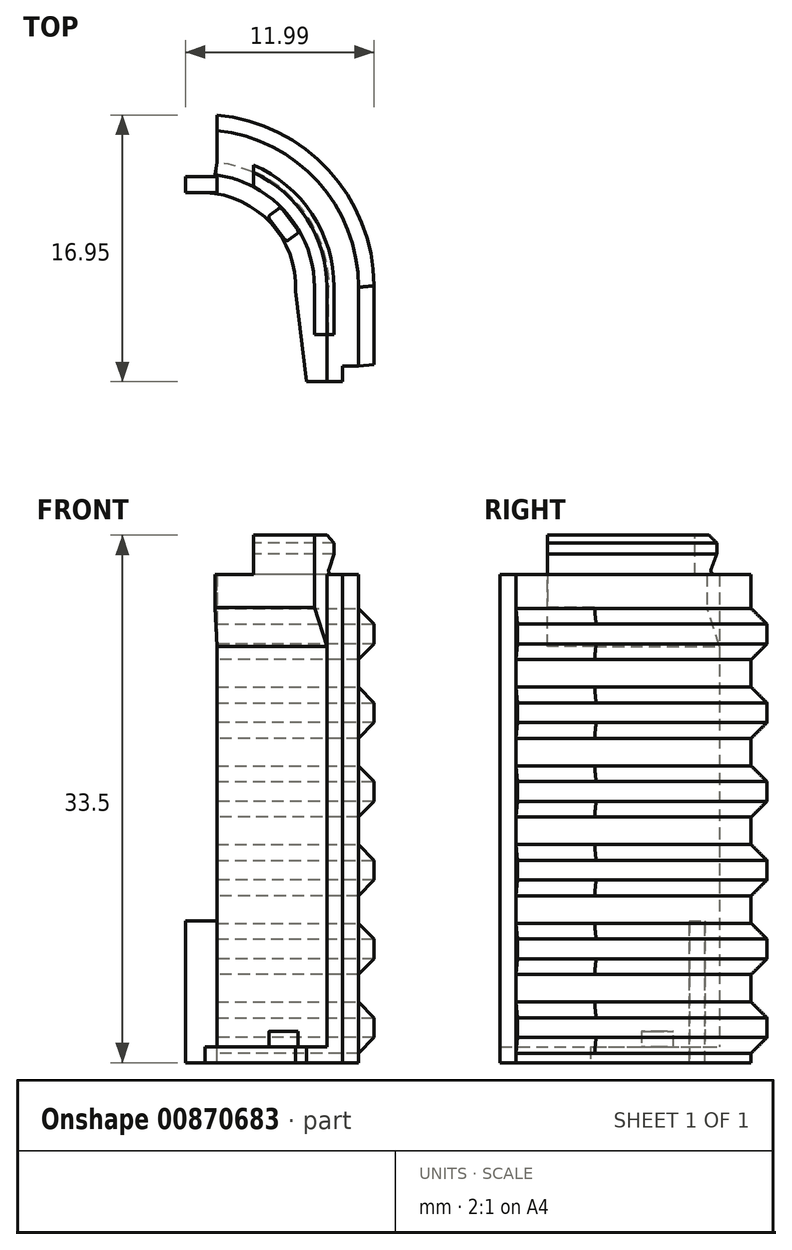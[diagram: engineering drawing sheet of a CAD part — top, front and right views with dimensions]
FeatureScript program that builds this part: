
annotation { "Feature Type Name" : "Feature", "Feature Type Description" : "" }
export const myFeature = defineFeature(function(context is Context, id is Id, definition is map)
    precondition{}
    {
        {
            var Q0;
            Q0=qCreatedBy(makeId("Top.planeOp"),FACE);
            var sketch = newSketch(context, id + "F0", { "sketchPlane" : qUnion([Q0])});
            skArc(sketch, "E0", {"start": v(10, 0) * mm, "mid": v(7.07, 7.07) * mm, "end": v(0, 10) * mm});
            skArc(sketch, "E1", {"start": v(8, 0) * mm, "mid": v(5.66, 5.66) * mm, "end": v(0, 8) * mm});
            skLineSegment(sketch, "E2", {"start": v(0, 8) * mm, "end": v(0, 10) * mm});
            skLineSegment(sketch, "E3.0", {"start": v(8, -5) * mm, "end": v(10, -5) * mm});
            skLineSegment(sketch, "E4", {"start": v(8, 0) * mm, "end": v(8, -5) * mm});
            skLineSegment(sketch, "E5", {"start": v(10, 0) * mm, "end": v(10, -5) * mm});
            skSolve(sketch);
        }
        {
            var Q0;
            Q0=makeQuery(id+"F0.imprint","IMPRINT",FACE,{"disambiguationData":[TD([[makeQuery(id+"F0.imprint","IMPRINT",EDGE,{"derivedFrom":sQuery(id+"F0.wireOp",EDGE,"E0")}),1.0]])]});
            extrude(context, id + "F1", {"entities" : qUnion([Q0]), "depth" : 31 * mm, "offsetDistance" : 25 * mm});
        }
        {
            var Q0;
            {var subQ0=sQuery(id+"F0.wireOp",EDGE,"E1");Q0=makeQuery(id+"FjqXergtBeOg1T9_1.boolean.opBoolean","MERGE",FACE,{"derivedFrom":[makeQuery(id+"F1.opExtrude","CAP_FACE",FACE,{"disambiguationData":[OSD([sQuery(id+"F0.wireOp",EDGE,"E0"),subQ0,sQuery(id+"F0.wireOp",EDGE,"E2"),sQuery(id+"F0.wireOp",EDGE,"4YHJIpGK-HOE4-qftu-6N1K-RQKpWv2yEjac")])],"isStart":false}),makeQuery(id+"FjqXergtBeOg1T9_1.opSweep","SWEPT_FACE",FACE,{"disambiguationData":[OSD([subQ0,sQuery(id+"F456tpTZeAtuVHj_1.wireOp",EDGE,"sk94qZU0-1xnX-XY7q-ALrQ-k9b9ehyhfIlW")])]})]});}
            var sketch = newSketch(context, id + "F2", { "sketchPlane" : qUnion([Q0])});
            skLineSegment(sketch, "E6.bottom", {"start": v(0, 10) * mm, "end": v(1, 10) * mm});
            skLineSegment(sketch, "E6.top", {"start": v(0, 9) * mm, "end": v(1, 9) * mm});
            skLineSegment(sketch, "E6.left", {"start": v(0, 10) * mm, "end": v(0, 9) * mm});
            skLineSegment(sketch, "E6.right", {"start": v(1, 10) * mm, "end": v(1, 9) * mm});
            skSolve(sketch);
        }
        {
            var Q0;
            {var subQ0=sQuery(id+"F2.wireOp",EDGE,"E6.top");Q0=makeQuery(id+"F2.imprint","IMPRINT",FACE,{"disambiguationData":[TD([[makeQuery(id+"F2.imprint","IMPRINT",EDGE,{"derivedFrom":subQ0}),1.0]])]});}
            extrude(context, id + "F3", {"entities" : qUnion([Q0]), "operationType" : NewBodyOperationType.REMOVE, "oppositeDirection" : true, "depth" : 33.9 * mm, "offsetDistance" : 25 * mm});
        }
        {
            var Q0;
            {var subQ0=sQuery(id+"F0.wireOp",EDGE,"E1");Q0=makeQuery(id+"FjqXergtBeOg1T9_1.boolean.opBoolean","MERGE",FACE,{"derivedFrom":[makeQuery(id+"F1.opExtrude","CAP_FACE",FACE,{"disambiguationData":[OSD([sQuery(id+"F0.wireOp",EDGE,"E0"),subQ0,sQuery(id+"F0.wireOp",EDGE,"E2"),sQuery(id+"F0.wireOp",EDGE,"4YHJIpGK-HOE4-qftu-6N1K-RQKpWv2yEjac")])],"isStart":false}),makeQuery(id+"FjqXergtBeOg1T9_1.opSweep","SWEPT_FACE",FACE,{"disambiguationData":[OSD([subQ0,sQuery(id+"F456tpTZeAtuVHj_1.wireOp",EDGE,"sk94qZU0-1xnX-XY7q-ALrQ-k9b9ehyhfIlW")])]})]});}
            var sketch = newSketch(context, id + "F4", { "sketchPlane" : qUnion([Q0])});
            skLineSegment(sketch, "E7.bottom", {"start": v(8, 0) * mm, "end": v(9, 0) * mm});
            skLineSegment(sketch, "E7.top", {"start": v(8, -1) * mm, "end": v(9, -1) * mm});
            skLineSegment(sketch, "E7.left", {"start": v(8, 0) * mm, "end": v(8, -1) * mm});
            skLineSegment(sketch, "E7.right", {"start": v(9, 0) * mm, "end": v(9, -1) * mm});
            skSolve(sketch);
        }
        {
            var Q0;
            Q0=makeQuery(id+"F4.imprint","IMPRINT",FACE,{"disambiguationData":[TD([[makeQuery(id+"F4.imprint","IMPRINT",EDGE,{"derivedFrom":sQuery(id+"F4.wireOp",EDGE,"E7.bottom")}),-1.0]])]});
            extrude(context, id + "F5", {"entities" : qUnion([Q0]), "operationType" : NewBodyOperationType.ADD, "oppositeDirection" : true, "depth" : 10 * mm, "offsetDistance" : 25 * mm});
        }
        {
            var Q0;
            Q0=makeQuery(id+"F1.opExtrude","CAP_FACE",FACE,{"disambiguationData":[OSD([sQuery(id+"F0.wireOp",EDGE,"E0"),sQuery(id+"F0.wireOp",EDGE,"E1"),sQuery(id+"F0.wireOp",EDGE,"E2"),sQuery(id+"F0.wireOp",EDGE,"4YHJIpGK-HOE4-qftu-6N1K-RQKpWv2yEjac")])],"isStart":true});
            var sketch = newSketch(context, id + "F6", { "sketchPlane" : qUnion([Q0])});
            skLineSegment(sketch, "E8.bottom", {"start": v(8, 0) * mm, "end": v(6, 0) * mm});
            skLineSegment(sketch, "E8.top", {"start": v(8, -0.5) * mm, "end": v(6, -0.5) * mm});
            skLineSegment(sketch, "E8.left", {"start": v(8, 0) * mm, "end": v(8, -0.5) * mm});
            skLineSegment(sketch, "E8.right", {"start": v(6, 0) * mm, "end": v(6, -0.5) * mm});
            skSolve(sketch);
        }
        {
            var Q0;
            {var subQ0=sQuery(id+"F6.wireOp",EDGE,"E8.bottom");Q0=makeQuery(id+"F6.imprint","IMPRINT",FACE,{"disambiguationData":[TD([[makeQuery(id+"F6.imprint","IMPRINT",EDGE,{"derivedFrom":subQ0}),1.0]])]});}
            extrude(context, id + "F7", {"entities" : qUnion([Q0]), "operationType" : NewBodyOperationType.REMOVE, "endBound" : BoundingType.SYMMETRIC, "oppositeDirection" : true, "depth" : 25 * mm, "offsetDistance" : 25 * mm});
        }
        {
            var Q0;
            Q0=makeQuery(id+"FmoRTXEpy4M3MYA_1.boolean.opBoolean","MERGE",FACE,{"derivedFrom":[makeQuery(id+"F3.boolean.opBoolean","COPY",FACE,{"derivedFrom":makeQuery(id+"F3.opExtrude","SWEPT_FACE",FACE,{"disambiguationData":[OSD([sQuery(id+"F2.wireOp",EDGE,"E6.right")])]})}),makeQuery(id+"FmoRTXEpy4M3MYA_1.opExtrude","SWEPT_FACE",FACE,{"disambiguationData":[OSD([sQuery(id+"FKi1AGYCDrlm84A_1.wireOp",EDGE,"uPgSb5Jb-cWgF-9LKH-gCYG-FSBK6ZN9CBQU.right")])]})]});
            var sketch = newSketch(context, id + "F8", { "sketchPlane" : qUnion([Q0])});
            skLineSegment(sketch, "E9", {"start": v(-9.95, 0.6) * mm, "end": v(-10.95, 1.6) * mm});
            skLineSegment(sketch, "E10", {"start": v(-10.95, 1.6) * mm, "end": v(-10.95, 2.85) * mm});
            skLineSegment(sketch, "E11", {"start": v(-10.95, 2.85) * mm, "end": v(-9.95, 3.85) * mm});
            skLineSegment(sketch, "E12.0.1.0", {"start": v(-10.95, 7.85) * mm, "end": v(-9.95, 8.85) * mm});
            skLineSegment(sketch, "E12.0.1.1", {"start": v(-10.95, 6.6) * mm, "end": v(-10.95, 7.85) * mm});
            skLineSegment(sketch, "E12.0.1.2", {"start": v(-9.95, 5.6) * mm, "end": v(-10.95, 6.6) * mm});
            skLineSegment(sketch, "E12.0.2.0", {"start": v(-10.95, 12.85) * mm, "end": v(-9.95, 13.85) * mm});
            skLineSegment(sketch, "E12.0.2.1", {"start": v(-10.95, 11.6) * mm, "end": v(-10.95, 12.85) * mm});
            skLineSegment(sketch, "E12.0.2.2", {"start": v(-9.95, 10.6) * mm, "end": v(-10.95, 11.6) * mm});
            skLineSegment(sketch, "E12.0.3.0", {"start": v(-10.95, 17.85) * mm, "end": v(-9.95, 18.85) * mm});
            skLineSegment(sketch, "E12.0.3.1", {"start": v(-10.95, 16.6) * mm, "end": v(-10.95, 17.85) * mm});
            skLineSegment(sketch, "E12.0.3.2", {"start": v(-9.95, 15.6) * mm, "end": v(-10.95, 16.6) * mm});
            skLineSegment(sketch, "E12.0.4.0", {"start": v(-10.95, 22.85) * mm, "end": v(-9.95, 23.85) * mm});
            skLineSegment(sketch, "E12.0.4.1", {"start": v(-10.95, 21.6) * mm, "end": v(-10.95, 22.85) * mm});
            skLineSegment(sketch, "E12.0.4.2", {"start": v(-9.95, 20.6) * mm, "end": v(-10.95, 21.6) * mm});
            skLineSegment(sketch, "E12.0.5.0", {"start": v(-10.95, 27.85) * mm, "end": v(-9.95, 28.85) * mm});
            skLineSegment(sketch, "E12.0.5.1", {"start": v(-10.95, 26.6) * mm, "end": v(-10.95, 27.85) * mm});
            skLineSegment(sketch, "E12.0.5.2", {"start": v(-9.95, 25.6) * mm, "end": v(-10.95, 26.6) * mm});
            skLineSegment(sketch, "E12.direction1", {"start": v(-9.95, 0.6) * mm, "end": v(15.05, 0.6) * mm, "construction": true});
            skLineSegment(sketch, "E12.direction2", {"start": v(-9.95, 0.6) * mm, "end": v(-9.95, 5.6) * mm, "construction": true});
            skSolve(sketch);
        }
        {
            var Q0;
            {var subQ0=sQuery(id+"F0.wireOp",EDGE,"E1");Q0=makeQuery(id+"FjqXergtBeOg1T9_1.boolean.opBoolean","MERGE",FACE,{"derivedFrom":[makeQuery(id+"F1.opExtrude","CAP_FACE",FACE,{"disambiguationData":[OSD([sQuery(id+"F0.wireOp",EDGE,"E0"),subQ0,sQuery(id+"F0.wireOp",EDGE,"E2"),sQuery(id+"F0.wireOp",EDGE,"E3.0"),sQuery(id+"F0.wireOp",EDGE,"E4"),sQuery(id+"F0.wireOp",EDGE,"E5")])],"isStart":false}),makeQuery(id+"FjqXergtBeOg1T9_1.opSweep","SWEPT_FACE",FACE,{"disambiguationData":[OSD([subQ0,sQuery(id+"F456tpTZeAtuVHj_1.wireOp",EDGE,"sk94qZU0-1xnX-XY7q-ALrQ-k9b9ehyhfIlW")])]})]});}
            var sketch = newSketch(context, id + "F9", { "sketchPlane" : qUnion([Q0])});
            skLineSegment(sketch, "E13.bottom", {"start": v(8, -5) * mm, "end": v(9, -5) * mm});
            skLineSegment(sketch, "E13.top", {"start": v(8, -6) * mm, "end": v(9, -6) * mm});
            skLineSegment(sketch, "E13.left", {"start": v(8, -5) * mm, "end": v(8, -6) * mm});
            skLineSegment(sketch, "E13.right", {"start": v(9, -5) * mm, "end": v(9, -6) * mm});
            skSolve(sketch);
        }
        {
            var Q0;
            Q0=makeQuery(id+"F9.imprint","IMPRINT",FACE,{"disambiguationData":[TD([[makeQuery(id+"F9.imprint","IMPRINT",EDGE,{"derivedFrom":sQuery(id+"F9.wireOp",EDGE,"CXyakN0J-a7iq-0E7a-vx4G-uZPd13JSKx8G.bottom")}),-1.0]])]});
            var Q1;
            Q1=makeQuery(id+"F9.imprint","IMPRINT",FACE,{"disambiguationData":[TD([[makeQuery(id+"F9.imprint","IMPRINT",EDGE,{"derivedFrom":sQuery(id+"F9.wireOp",EDGE,"E13.bottom")}),-1.0]])]});
            extrude(context, id + "F10", {"entities" : qUnion([Q0, Q1]), "operationType" : NewBodyOperationType.ADD, "oppositeDirection" : true, "depth" : 31 * mm, "offsetDistance" : 25 * mm});
        }
        {
            var Q0;
            {var subQ0=sQuery(id+"F2.wireOp",EDGE,"E6.right");var subQ1=sQuery(id+"F0.wireOp",EDGE,"E5");var subQ2=sQuery(id+"F0.wireOp",EDGE,"E4");var subQ3=sQuery(id+"F0.wireOp",EDGE,"E3.0");var subQ4=sQuery(id+"F0.wireOp",EDGE,"E2");var subQ5=sQuery(id+"F0.wireOp",EDGE,"E1");var subQ6=sQuery(id+"F0.wireOp",EDGE,"E0");Q0=makeQuery(id+"F17.boolean.opBoolean","MERGE",FACE,{"derivedFrom":[makeQuery(id+"FmoRTXEpy4M3MYA_1.boolean.opBoolean","MERGE",FACE,{"derivedFrom":[makeQuery(id+"F3.boolean.opBoolean","COPY",FACE,{"derivedFrom":makeQuery(id+"F3.opExtrude","SWEPT_FACE",FACE,{"disambiguationData":[OSD([subQ0])]})}),makeQuery(id+"FmoRTXEpy4M3MYA_1.opExtrude","SWEPT_FACE",FACE,{"disambiguationData":[OSD([sQuery(id+"FKi1AGYCDrlm84A_1.wireOp",EDGE,"uPgSb5Jb-cWgF-9LKH-gCYG-FSBK6ZN9CBQU.right")])]})]}),makeQuery(id+"F17.opSweep","CAP_FACE",FACE,{"disambiguationData":[OSD([subQ6,subQ5,subQ4,subQ3,subQ2,subQ1,subQ0,sQuery(id+"F8.wireOp",EDGE,"E9"),sQuery(id+"F8.wireOp",EDGE,"E10"),sQuery(id+"F8.wireOp",EDGE,"E11")])],"isStart":true}),makeQuery(id+"F17.opSweep","CAP_FACE",FACE,{"disambiguationData":[OSD([subQ6,subQ5,subQ4,subQ3,subQ2,subQ1,subQ0,sQuery(id+"F8.wireOp",EDGE,"9e4cff42-fbfe-4d5b-8348-393125ff6e66"),sQuery(id+"F8.wireOp",EDGE,"96184abe-4f2f-4861-a6de-bc5c8fcc41ba"),sQuery(id+"F8.wireOp",EDGE,"648e9435-4f86-4073-b577-d57563a5dedb"),sQuery(id+"F8.wireOp",EDGE,"d1ab4f86-afde-471a-a081-81eba838b778")])],"isStart":true}),makeQuery(id+"F17.opSweep","CAP_FACE",FACE,{"disambiguationData":[OSD([subQ6,subQ5,subQ4,subQ3,subQ2,subQ1,subQ0,sQuery(id+"F8.wireOp",EDGE,"44abebc7-ddca-4564-8f04-e84f1205f6d8"),sQuery(id+"F8.wireOp",EDGE,"33028e05-cfbc-4c81-b8d7-78fda016a80c"),sQuery(id+"F8.wireOp",EDGE,"75f7a074-1fce-462e-93cf-1e88678016c3"),sQuery(id+"F8.wireOp",EDGE,"17611aa9-75d6-4124-ba45-961e49a3dcaa")])],"isStart":true}),makeQuery(id+"F17.opSweep","CAP_FACE",FACE,{"disambiguationData":[OSD([subQ6,subQ5,subQ4,subQ3,subQ2,subQ1,subQ0,sQuery(id+"F8.wireOp",EDGE,"57387fe9-113e-4e5e-88a7-aafb975e1367"),sQuery(id+"F8.wireOp",EDGE,"880b83f9-7a74-47bf-9483-38739a431fbb"),sQuery(id+"F8.wireOp",EDGE,"a894a9b4-4521-4225-9b02-249f6e3a631f"),sQuery(id+"F8.wireOp",EDGE,"36acd7d2-b939-4856-b06f-7314ead4a0f2")])],"isStart":true})]});}
            var sketch = newSketch(context, id + "F11", { "sketchPlane" : qUnion([Q0])});
            skLineSegment(sketch, "E14", {"start": v(-7.94, 1) * mm, "end": v(-5.94, 1) * mm});
            skLineSegment(sketch, "E15", {"start": v(-5.94, 1) * mm, "end": v(-5.94, 0) * mm});
            skLineSegment(sketch, "E16", {"start": v(-5.94, 0) * mm, "end": v(-7.94, 0) * mm});
            skLineSegment(sketch, "E17", {"start": v(-7.94, 1) * mm, "end": v(-7.94, 0) * mm});
            skSolve(sketch);
        }
        {
            var Q0;
            Q0=makeQuery(id+"F10.boolean.opBoolean","MERGE",FACE,{"derivedFrom":[makeQuery(id+"F1.opExtrude","CAP_FACE",FACE,{"disambiguationData":[OSD([sQuery(id+"F0.wireOp",EDGE,"E0"),sQuery(id+"F0.wireOp",EDGE,"E1"),sQuery(id+"F0.wireOp",EDGE,"E2"),sQuery(id+"F0.wireOp",EDGE,"E3.0"),sQuery(id+"F0.wireOp",EDGE,"E4"),sQuery(id+"F0.wireOp",EDGE,"E5")])],"isStart":false}),makeQuery(id+"F10.opExtrude","CAP_FACE",FACE,{"disambiguationData":[OSD([sQuery(id+"F9.wireOp",EDGE,"CXyakN0J-a7iq-0E7a-vx4G-uZPd13JSKx8G.bottom"),sQuery(id+"F9.wireOp",EDGE,"CXyakN0J-a7iq-0E7a-vx4G-uZPd13JSKx8G.top"),sQuery(id+"F9.wireOp",EDGE,"CXyakN0J-a7iq-0E7a-vx4G-uZPd13JSKx8G.left"),sQuery(id+"F9.wireOp",EDGE,"CXyakN0J-a7iq-0E7a-vx4G-uZPd13JSKx8G.right")])],"isStart":true})]});
            var sketch = newSketch(context, id + "F12", { "sketchPlane" : qUnion([Q0])});
            skLineSegment(sketch, "E18.bottom", {"start": v(1, 9) * mm, "end": v(1, 9) * mm});
            skLineSegment(sketch, "E18.top", {"start": v(1, 4.94) * mm, "end": v(1, 4.94) * mm});
            skLineSegment(sketch, "E18.left", {"start": v(1, 9) * mm, "end": v(1, 4.94) * mm});
            skLineSegment(sketch, "E18.right", {"start": v(1, 9) * mm, "end": v(1, 4.94) * mm});
            skLineSegment(sketch, "E19", {"start": v(1, 4.94) * mm, "end": v(-1.52, 4.94) * mm});
            skLineSegment(sketch, "E20", {"start": v(-1.52, 4.94) * mm, "end": v(-1.52, 9) * mm});
            skLineSegment(sketch, "E21", {"start": v(-1.52, 9) * mm, "end": v(1, 9) * mm});
            skSolve(sketch);
        }
        {
            var Q0;
            {var subQ5=makeQuery(id+"F1.opExtrude","CAP_EDGE",EDGE,{"disambiguationData":[OSD([sQuery(id+"F0.wireOp",EDGE,"E2")])],"isStart":false});Q0=makeQuery(id+"F12.imprint","IMPRINT",FACE,{"disambiguationData":[TD([[makeQuery(id+"F12.imprint","IMPRINT",EDGE,{"derivedFrom":subQ5}),-1.0]])]});}
            var Q1;
            {var subQ6=sQuery(id+"F12.wireOp",EDGE,"E19");Q1=makeQuery(id+"F12.imprint","IMPRINT",FACE,{"disambiguationData":[TD([[makeQuery(id+"F12.imprint","IMPRINT",EDGE,{"derivedFrom":subQ6}),-1.0]])]});}
            extrude(context, id + "F13", {"entities" : qUnion([Q0, Q1]), "operationType" : NewBodyOperationType.REMOVE, "oppositeDirection" : true, "depth" : 22 * mm, "offsetDistance" : 25 * mm});
        }
        {
            var Q0;
            {var subQ0=sQuery(id+"F0.wireOp",EDGE,"E4");Q0=makeQuery(id+"F16.boolean.opBoolean","MERGE",FACE,{"derivedFrom":[makeQuery(id+"F10.boolean.opBoolean","MERGE",FACE,{"derivedFrom":[makeQuery(id+"F1.opExtrude","CAP_FACE",FACE,{"disambiguationData":[OSD([sQuery(id+"F0.wireOp",EDGE,"E0"),sQuery(id+"F0.wireOp",EDGE,"E1"),sQuery(id+"F0.wireOp",EDGE,"E2"),sQuery(id+"F0.wireOp",EDGE,"E3.0"),subQ0,sQuery(id+"F0.wireOp",EDGE,"E5")])],"isStart":true}),makeQuery(id+"F10.opExtrude","CAP_FACE",FACE,{"disambiguationData":[OSD([sQuery(id+"F9.wireOp",EDGE,"CXyakN0J-a7iq-0E7a-vx4G-uZPd13JSKx8G.bottom"),sQuery(id+"F9.wireOp",EDGE,"CXyakN0J-a7iq-0E7a-vx4G-uZPd13JSKx8G.top"),sQuery(id+"F9.wireOp",EDGE,"CXyakN0J-a7iq-0E7a-vx4G-uZPd13JSKx8G.left"),sQuery(id+"F9.wireOp",EDGE,"CXyakN0J-a7iq-0E7a-vx4G-uZPd13JSKx8G.right")])],"isStart":false})]}),makeQuery(id+"F16.opSweep","SWEPT_FACE",FACE,{"disambiguationData":[OSD([subQ0,sQuery(id+"F11.wireOp",EDGE,"E16")])]})]});}
            var sketch = newSketch(context, id + "F14", { "sketchPlane" : qUnion([Q0])});
            skLineSegment(sketch, "E22.bottom", {"start": v(9, 5) * mm, "end": v(4.55, 5) * mm});
            skLineSegment(sketch, "E22.top", {"start": v(9, 6.45) * mm, "end": v(4.55, 6.45) * mm});
            skLineSegment(sketch, "E22.left", {"start": v(9, 5) * mm, "end": v(9, 6.45) * mm});
            skLineSegment(sketch, "E22.right", {"start": v(4.55, 5) * mm, "end": v(4.55, 6.45) * mm});
            skSolve(sketch);
        }
        {
            var Q0;
            {var subQ1=sQuery(id+"F11.wireOp",EDGE,"E16");var subQ2=sQuery(id+"F0.wireOp",EDGE,"E4");var subQ3=makeQuery(id+"F16.opSweep","CAP_EDGE",EDGE,{"disambiguationData":[OSD([sQuery(id+"F0.wireOp",EDGE,"E3.0"),subQ2,subQ1])],"isStart":true});Q0=makeQuery(id+"F14.imprint","IMPRINT",FACE,{"disambiguationData":[TD([[makeQuery(id+"F14.imprint","IMPRINT",EDGE,{"derivedFrom":subQ3}),1.0]])]});}
            var Q1;
            {var subQ4=sQuery(id+"F14.wireOp",EDGE,"E22.top");Q1=makeQuery(id+"F14.imprint","IMPRINT",FACE,{"disambiguationData":[TD([[makeQuery(id+"F14.imprint","IMPRINT",EDGE,{"derivedFrom":subQ4}),1.0]])]});}
            extrude(context, id + "F15", {"entities" : qUnion([Q0, Q1]), "operationType" : NewBodyOperationType.REMOVE, "oppositeDirection" : true, "depth" : 25 * mm, "offsetDistance" : 25 * mm});
        }
        {
            var Q0;
            Q0=makeQuery(id+"F11.imprint","IMPRINT",FACE,{"disambiguationData":[TD([[makeQuery(id+"F11.imprint","IMPRINT",EDGE,{"derivedFrom":sQuery(id+"F11.wireOp",EDGE,"E14")}),-1.0]])]});
            var Q1;
            Q1=makeQuery(id+"F1.opExtrude","CAP_EDGE",EDGE,{"disambiguationData":[OSD([sQuery(id+"F0.wireOp",EDGE,"E1")])],"isStart":true});
            var Q2;
            Q2=makeQuery(id+"F1.opExtrude","CAP_EDGE",EDGE,{"disambiguationData":[OSD([sQuery(id+"F0.wireOp",EDGE,"E4")])],"isStart":true});
            sweep(context, id + "F16", {"operationType" : NewBodyOperationType.ADD, "profiles" : qUnion([Q0]), "path" : qUnion([Q1, Q2])});
        }
        {
            var Q0;
            {var subQ0=sQuery(id+"F8.wireOp",EDGE,"E9");Q0=makeQuery(id+"F8.imprint","IMPRINT",FACE,{"disambiguationData":[TD([[makeQuery(id+"F8.imprint","IMPRINT",EDGE,{"derivedFrom":subQ0}),-1.0]])]});}
            var Q1;
            Q1=makeQuery(id+"F8.imprint","IMPRINT",FACE,{"disambiguationData":[TD([[makeQuery(id+"F8.imprint","IMPRINT",EDGE,{"derivedFrom":sQuery(id+"F8.wireOp",EDGE,"9e4cff42-fbfe-4d5b-8348-393125ff6e66")}),-1.0]])]});
            var Q2;
            Q2=makeQuery(id+"F8.imprint","IMPRINT",FACE,{"disambiguationData":[TD([[makeQuery(id+"F8.imprint","IMPRINT",EDGE,{"derivedFrom":sQuery(id+"F8.wireOp",EDGE,"44abebc7-ddca-4564-8f04-e84f1205f6d8")}),-1.0]])]});
            var Q3;
            Q3=makeQuery(id+"F8.imprint","IMPRINT",FACE,{"disambiguationData":[TD([[makeQuery(id+"F8.imprint","IMPRINT",EDGE,{"derivedFrom":sQuery(id+"F8.wireOp",EDGE,"57387fe9-113e-4e5e-88a7-aafb975e1367")}),-1.0]])]});
            var Q4;
            {var subQ0=sQuery(id+"F8.wireOp",EDGE,"E12.0.1.0");Q4=makeQuery(id+"F8.imprint","IMPRINT",FACE,{"disambiguationData":[TD([[makeQuery(id+"F8.imprint","IMPRINT",EDGE,{"derivedFrom":subQ0}),-1.0]])]});}
            var Q5;
            {var subQ0=sQuery(id+"F8.wireOp",EDGE,"E12.0.2.0");Q5=makeQuery(id+"F8.imprint","IMPRINT",FACE,{"disambiguationData":[TD([[makeQuery(id+"F8.imprint","IMPRINT",EDGE,{"derivedFrom":subQ0}),-1.0]])]});}
            var Q6;
            {var subQ0=sQuery(id+"F8.wireOp",EDGE,"E12.0.3.0");Q6=makeQuery(id+"F8.imprint","IMPRINT",FACE,{"disambiguationData":[TD([[makeQuery(id+"F8.imprint","IMPRINT",EDGE,{"derivedFrom":subQ0}),-1.0]])]});}
            var Q7;
            {var subQ0=sQuery(id+"F8.wireOp",EDGE,"E12.0.4.0");Q7=makeQuery(id+"F8.imprint","IMPRINT",FACE,{"disambiguationData":[TD([[makeQuery(id+"F8.imprint","IMPRINT",EDGE,{"derivedFrom":subQ0}),-1.0]])]});}
            var Q8;
            {var subQ0=sQuery(id+"F8.wireOp",EDGE,"E12.0.5.0");Q8=makeQuery(id+"F8.imprint","IMPRINT",FACE,{"disambiguationData":[TD([[makeQuery(id+"F8.imprint","IMPRINT",EDGE,{"derivedFrom":subQ0}),-1.0]])]});}
            var Q9;
            Q9=makeQuery(id+"F1.opExtrude","CAP_EDGE",EDGE,{"disambiguationData":[OSD([sQuery(id+"F0.wireOp",EDGE,"E0")])],"isStart":true});
            var Q10;
            Q10=makeQuery(id+"F1.opExtrude","CAP_EDGE",EDGE,{"disambiguationData":[OSD([sQuery(id+"F0.wireOp",EDGE,"E5")])],"isStart":true});
            sweep(context, id + "F17", {"operationType" : NewBodyOperationType.ADD, "profiles" : qUnion([Q0, Q1, Q2, Q3, Q4, Q5, Q6, Q7, Q8]), "path" : qUnion([Q9, Q10])});
        }
        {
            var Q0;
            {var subQ0=sQuery(id+"F9.wireOp",EDGE,"E13.left");var subQ1=sQuery(id+"F0.wireOp",EDGE,"E4");Q0=makeQuery(id+"F16.boolean.opBoolean","MERGE",FACE,{"derivedFrom":[makeQuery(id+"F10.boolean.opBoolean","MERGE",FACE,{"derivedFrom":[makeQuery(id+"F1.opExtrude","CAP_FACE",FACE,{"disambiguationData":[OSD([sQuery(id+"F0.wireOp",EDGE,"E0"),sQuery(id+"F0.wireOp",EDGE,"E1"),sQuery(id+"F0.wireOp",EDGE,"E2"),sQuery(id+"F0.wireOp",EDGE,"E3.0"),subQ1,sQuery(id+"F0.wireOp",EDGE,"E5")])],"isStart":true}),makeQuery(id+"F10.opExtrude","CAP_FACE",FACE,{"disambiguationData":[OSD([sQuery(id+"F9.wireOp",EDGE,"E13.bottom"),sQuery(id+"F9.wireOp",EDGE,"E13.top"),subQ0,sQuery(id+"F9.wireOp",EDGE,"E13.right")])],"isStart":false})]}),makeQuery(id+"F16.opSweep","SWEPT_FACE",FACE,{"disambiguationData":[OSD([subQ1,subQ0,sQuery(id+"F11.wireOp",EDGE,"E16")])]})]});}
            var sketch = newSketch(context, id + "F18", { "sketchPlane" : qUnion([Q0])});
            skLineSegment(sketch, "E23.bottom", {"start": v(9, 6) * mm, "end": v(4.51, 6) * mm});
            skLineSegment(sketch, "E23.top", {"start": v(9, 7.29) * mm, "end": v(4.51, 7.29) * mm});
            skLineSegment(sketch, "E23.left", {"start": v(9, 6) * mm, "end": v(9, 7.29) * mm});
            skLineSegment(sketch, "E23.right", {"start": v(4.51, 6) * mm, "end": v(4.51, 7.29) * mm});
            skSolve(sketch);
        }
        {
            var Q0;
            {var subQ1=sQuery(id+"F11.wireOp",EDGE,"E16");var subQ2=sQuery(id+"F9.wireOp",EDGE,"E13.left");var subQ3=makeQuery(id+"F16.opSweep","CAP_EDGE",EDGE,{"disambiguationData":[OSD([sQuery(id+"F9.wireOp",EDGE,"E13.top"),subQ2,subQ1])],"isStart":true});Q0=makeQuery(id+"F18.imprint","IMPRINT",FACE,{"disambiguationData":[TD([[makeQuery(id+"F18.imprint","IMPRINT",EDGE,{"derivedFrom":subQ3}),1.0]])]});}
            var Q1;
            Q1=makeQuery(id+"F18.imprint","IMPRINT",FACE,{"disambiguationData":[TD([[makeQuery(id+"F18.imprint","IMPRINT",EDGE,{"derivedFrom":sQuery(id+"F18.wireOp",EDGE,"E23.top")}),1.0]])]});
            extrude(context, id + "F19", {"entities" : qUnion([Q0, Q1]), "operationType" : NewBodyOperationType.REMOVE, "oppositeDirection" : true, "depth" : 25 * mm, "offsetDistance" : 25 * mm});
        }
        {
            var Q0;
            Q0=makeQuery(id+"F16.opSweep","SWEPT_FACE",FACE,{"disambiguationData":[OSD([sQuery(id+"F0.wireOp",EDGE,"E4"),sQuery(id+"F9.wireOp",EDGE,"E13.left"),sQuery(id+"F11.wireOp",EDGE,"E14")])]});
            var sketch = newSketch(context, id + "F20", { "sketchPlane" : qUnion([Q0])});
            skLineSegment(sketch, "E24", {"start": v(0.25, 6.02) * mm, "end": v(0, 6.02) * mm});
            skLineSegment(sketch, "E25", {"start": v(0, 8) * mm, "end": v(0, 6.02) * mm});
            skLineSegment(sketch, "E26", {"start": v(0, 8) * mm, "end": v(0.25, 6.02) * mm});
            skSolve(sketch);
        }
        {
            var Q0;
            Q0=makeQuery(id+"F20.imprint","IMPRINT",FACE,{"disambiguationData":[TD([[makeQuery(id+"F20.imprint","IMPRINT",EDGE,{"derivedFrom":sQuery(id+"F20.wireOp",EDGE,"E24")}),-1.0]])]});
            extrude(context, id + "F21", {"entities" : qUnion([Q0]), "operationType" : NewBodyOperationType.ADD, "oppositeDirection" : true, "depth" : 1 * mm, "offsetDistance" : 25 * mm});
        }
        {
            var Q0;
            Q0=makeQuery(id+"F13.boolean.opBoolean","COPY",FACE,{"derivedFrom":makeQuery(id+"F13.opExtrude","CAP_FACE",FACE,{"disambiguationData":[OSD([sQuery(id+"F12.wireOp",EDGE,"E18.right"),sQuery(id+"F12.wireOp",EDGE,"E19"),sQuery(id+"F12.wireOp",EDGE,"E20"),sQuery(id+"F12.wireOp",EDGE,"E21")])],"isStart":false})});
            var sketch = newSketch(context, id + "F22", { "sketchPlane" : qUnion([Q0])});
            skLineSegment(sketch, "E27.bottom", {"start": v(0, 9) * mm, "end": v(1, 9) * mm});
            skLineSegment(sketch, "E27.top", {"start": v(0, 7.58) * mm, "end": v(1, 7.58) * mm});
            skLineSegment(sketch, "E27.left", {"start": v(0, 9) * mm, "end": v(0, 7.58) * mm});
            skLineSegment(sketch, "E27.right", {"start": v(1, 9) * mm, "end": v(1, 7.58) * mm});
            skSolve(sketch);
        }
        {
            var Q0;
            {var subQ0=sQuery(id+"F22.wireOp",EDGE,"E27.bottom");Q0=makeQuery(id+"F22.imprint","IMPRINT",FACE,{"disambiguationData":[TD([[makeQuery(id+"F22.imprint","IMPRINT",EDGE,{"derivedFrom":subQ0}),-1.0]])]});}
            extrude(context, id + "F23", {"entities" : qUnion([Q0]), "operationType" : NewBodyOperationType.REMOVE, "oppositeDirection" : true, "depth" : 9 * mm, "offsetDistance" : 25 * mm});
        }
        {
            var Q0;
            Q0=makeQuery(id+"F21.boolean.opBoolean","MERGE",FACE,{"derivedFrom":[makeQuery(id+"F16.opSweep","SWEPT_FACE",FACE,{"disambiguationData":[OSD([sQuery(id+"F0.wireOp",EDGE,"E4"),sQuery(id+"F9.wireOp",EDGE,"E13.left"),sQuery(id+"F11.wireOp",EDGE,"E14")])]}),makeQuery(id+"F21.opExtrude","CAP_FACE",FACE,{"disambiguationData":[OSD([sQuery(id+"F20.wireOp",EDGE,"E24"),sQuery(id+"F20.wireOp",EDGE,"E25"),sQuery(id+"F20.wireOp",EDGE,"E26")])],"isStart":true})]});
            var sketch = newSketch(context, id + "F24", { "sketchPlane" : qUnion([Q0])});
            skLineSegment(sketch, "E28.right", {"start": v(1, 6.02) * mm, "end": v(1, 7.02) * mm});
            skLineSegment(sketch, "E29.right", {"start": v(-1, 6.02) * mm, "end": v(-1, 7.02) * mm});
            skLineSegment(sketch, "E30", {"start": v(-1, 7.02) * mm, "end": v(1, 7.02) * mm});
            skLineSegment(sketch, "E31", {"start": v(-1, 6.02) * mm, "end": v(1, 6.02) * mm});
            skSolve(sketch);
        }
        {
            var Q0;
            {var subQ2=sQuery(id+"F24.wireOp",EDGE,"E28.right");Q0=makeQuery(id+"F24.imprint","IMPRINT",FACE,{"disambiguationData":[TD([[makeQuery(id+"F24.imprint","IMPRINT",EDGE,{"derivedFrom":subQ2}),1.0]])]});}
            var Q1;
            {var subQ0=sQuery(id+"F24.wireOp",EDGE,"E29.right");Q1=makeQuery(id+"F24.imprint","IMPRINT",FACE,{"disambiguationData":[TD([[makeQuery(id+"F24.imprint","IMPRINT",EDGE,{"derivedFrom":subQ0}),-1.0]])]});}
            extrude(context, id + "F25", {"entities" : qUnion([Q0, Q1]), "operationType" : NewBodyOperationType.ADD, "depth" : 8 * mm, "offsetDistance" : 25 * mm});
        }
        {
            var Q0;
            Q0=makeQuery(id+"F19.boolean.opBoolean","MERGE",FACE,{"derivedFrom":[makeQuery(id+"F10.opExtrude","SWEPT_FACE",FACE,{"disambiguationData":[OSD([sQuery(id+"F9.wireOp",EDGE,"E13.top")])]}),makeQuery(id+"F19.opExtrude","SWEPT_FACE",FACE,{"disambiguationData":[OSD([sQuery(id+"F18.wireOp",EDGE,"E23.bottom")])]})]});
            var sketch = newSketch(context, id + "F26", { "sketchPlane" : qUnion([Q0])});
            skLineSegment(sketch, "E32", {"start": v(8, 26.44) * mm, "end": v(7.2, 28.9) * mm});
            skLineSegment(sketch, "E33", {"start": v(7.2, 28.9) * mm, "end": v(7.2, 33.38) * mm});
            skLineSegment(sketch, "E34", {"start": v(8, 26.44) * mm, "end": v(8, 31) * mm});
            skLineSegment(sketch, "E35", {"start": v(8, 31) * mm, "end": v(8, 31) * mm});
            skLineSegment(sketch, "E36", {"start": v(8, 31) * mm, "end": v(8.45, 32.3) * mm});
            skLineSegment(sketch, "E37", {"start": v(8.45, 32.3) * mm, "end": v(8.45, 33) * mm});
            skLineSegment(sketch, "E38", {"start": v(8.45, 33) * mm, "end": v(8, 33.5) * mm});
            skLineSegment(sketch, "E39", {"start": v(8, 33.5) * mm, "end": v(7.2, 33.5) * mm});
            skLineSegment(sketch, "E40", {"start": v(7.2, 33.5) * mm, "end": v(7.2, 33.15) * mm});
            skSolve(sketch);
        }
        {
            var Q0;
            Q0=makeQuery(id+"F26.imprint","IMPRINT",FACE,{"disambiguationData":[TD([[makeQuery(id+"F26.imprint","IMPRINT",EDGE,{"derivedFrom":sQuery(id+"F26.wireOp",EDGE,"E32")}),-1.0]])]});
            extrude(context, id + "F27", {"entities" : qUnion([Q0]), "operationType" : NewBodyOperationType.ADD, "oppositeDirection" : true, "depth" : 6 * mm, "offsetDistance" : 25 * mm});
        }
        {
            var Q0;
            Q0 = qSketchRegion(id + "F26", true);
            extrude(context, id + "F28", {"entities" : qUnion([Q0]), "operationType" : NewBodyOperationType.REMOVE, "oppositeDirection" : true, "depth" : 3 * mm, "offsetDistance" : 25 * mm});
        }
        {
            var Q0;
            Q0=makeQuery(id+"F25.opExtrude","CAP_FACE",FACE,{"disambiguationData":[OSD([sQuery(id+"F20.wireOp",EDGE,"E25"),sQuery(id+"F24.wireOp",EDGE,"E29.bottom"),sQuery(id+"F24.wireOp",EDGE,"E29.top"),sQuery(id+"F24.wireOp",EDGE,"E29.right")])],"isStart":true});
            extrude(context, id + "F29", {"entities" : qUnion([Q0]), "depth" : 1 * mm, "offsetDistance" : 25 * mm});
        }
        {
            var Q0;
            Q0=makeQuery(id+"F29.opExtrude","SWEPT_BODY",BODY,{"disambiguationData":[OSD([sQuery(id+"F20.wireOp",EDGE,"E25"),sQuery(id+"F24.wireOp",EDGE,"E29.bottom"),sQuery(id+"F24.wireOp",EDGE,"E29.top"),sQuery(id+"F24.wireOp",EDGE,"E29.right")])]});
            var Q1;
            Q1=makeQuery(id+"F25.opExtrude","SWEPT_BODY",BODY,{"disambiguationData":[OSD([sQuery(id+"F20.wireOp",EDGE,"E25"),sQuery(id+"F24.wireOp",EDGE,"E29.bottom"),sQuery(id+"F24.wireOp",EDGE,"E29.top"),sQuery(id+"F24.wireOp",EDGE,"E29.right")])]});
            var Q2;
            Q2=makeQuery(id+"F1.opExtrude","SWEPT_BODY",BODY,{"disambiguationData":[OSD([sQuery(id+"F0.wireOp",EDGE,"E0"),sQuery(id+"F0.wireOp",EDGE,"E1"),sQuery(id+"F0.wireOp",EDGE,"E2"),sQuery(id+"F0.wireOp",EDGE,"E3.0"),sQuery(id+"F0.wireOp",EDGE,"E4"),sQuery(id+"F0.wireOp",EDGE,"E5")])]});
            booleanBodies(context, id + "F30", {"operationType" : BooleanOperationType.UNION, "tools" : qUnion([Q0, Q1, Q2])});
        }
        {
            var Q0;
            Q0=makeQuery(id+"F21.boolean.opBoolean","MERGE",FACE,{"derivedFrom":[makeQuery(id+"F16.opSweep","SWEPT_FACE",FACE,{"disambiguationData":[OSD([sQuery(id+"F0.wireOp",EDGE,"E4"),sQuery(id+"F9.wireOp",EDGE,"E13.left"),sQuery(id+"F11.wireOp",EDGE,"E14")])]}),makeQuery(id+"F21.opExtrude","CAP_FACE",FACE,{"disambiguationData":[OSD([sQuery(id+"F20.wireOp",EDGE,"E24"),sQuery(id+"F20.wireOp",EDGE,"E25"),sQuery(id+"F20.wireOp",EDGE,"E26")])],"isStart":true})]});
            var sketch = newSketch(context, id + "F31", { "sketchPlane" : qUnion([Q0])});
            skLineSegment(sketch, "E41.bottom", {"start": v(0, 7.02) * mm, "end": v(1, 7.02) * mm});
            skLineSegment(sketch, "E41.top", {"start": v(0, 10.96) * mm, "end": v(1, 10.96) * mm});
            skLineSegment(sketch, "E41.left", {"start": v(0, 7.02) * mm, "end": v(0, 10.96) * mm});
            skLineSegment(sketch, "E41.right", {"start": v(1, 7.02) * mm, "end": v(1, 10.96) * mm});
            skSolve(sketch);
        }
        {
            var Q0;
            {var subQ0=sQuery(id+"F31.wireOp",EDGE,"E41.bottom");Q0=makeQuery(id+"F31.imprint","IMPRINT",FACE,{"disambiguationData":[TD([[makeQuery(id+"F31.imprint","IMPRINT",EDGE,{"derivedFrom":subQ0}),1.0]])]});}
            var Q1;
            {var subQ0=sQuery(id+"F31.wireOp",EDGE,"E41.top");Q1=makeQuery(id+"F31.imprint","IMPRINT",FACE,{"disambiguationData":[TD([[makeQuery(id+"F31.imprint","IMPRINT",EDGE,{"derivedFrom":subQ0}),-1.0]])]});}
            extrude(context, id + "F32", {"entities" : qUnion([Q0, Q1]), "operationType" : NewBodyOperationType.REMOVE, "oppositeDirection" : true, "depth" : 25 * mm, "offsetDistance" : 25 * mm});
        }
        {
            var Q0;
            Q0=makeQuery(id+"F28.boolean.opBoolean","COPY",FACE,{"derivedFrom":makeQuery(id+"F28.opExtrude","CAP_FACE",FACE,{"disambiguationData":[OSD([sQuery(id+"F26.wireOp",EDGE,"E32"),sQuery(id+"F26.wireOp",EDGE,"E33"),sQuery(id+"F26.wireOp",EDGE,"E34"),sQuery(id+"F26.wireOp",EDGE,"E36"),sQuery(id+"F26.wireOp",EDGE,"E37"),sQuery(id+"F26.wireOp",EDGE,"E38"),sQuery(id+"F26.wireOp",EDGE,"E39"),sQuery(id+"F26.wireOp",EDGE,"E40")])],"isStart":false})});
            var Q1;
            Q1=makeQuery(id+"F28.boolean.opBoolean","SPLIT",EDGE,{"derivedFrom":makeQuery(id+"F27.boolean.opBoolean","MERGE",EDGE,{"derivedFrom":[makeQuery(id+"F10.boolean.opBoolean","MERGE",EDGE,{"derivedFrom":[makeQuery(id+"F1.opExtrude","CAP_EDGE",EDGE,{"disambiguationData":[OSD([sQuery(id+"F0.wireOp",EDGE,"E4")])],"isStart":false}),makeQuery(id+"F10.opExtrude","CAP_EDGE",EDGE,{"disambiguationData":[OSD([sQuery(id+"F9.wireOp",EDGE,"E13.left")])],"isStart":true})]}),makeQuery(id+"F27.opExtrude","SWEPT_EDGE",EDGE,{"disambiguationData":[OSD([sQuery(id+"F9.wireOp",EDGE,"E13.top"),sQuery(id+"F26.wireOp",EDGE,"E34"),sQuery(id+"F26.wireOp",EDGE,"E36")])]})]})});
            var Q2;
            Q2=makeQuery(id+"F1.opExtrude","CAP_EDGE",EDGE,{"disambiguationData":[OSD([sQuery(id+"F0.wireOp",EDGE,"E1")])],"isStart":false});
            sweep(context, id + "F33", {"operationType" : NewBodyOperationType.ADD, "profiles" : qUnion([Q0]), "path" : qUnion([Q1, Q2])});
        }
        {
            var Q0;
            Q0=makeQuery(id+"F10.boolean.opBoolean","MERGE",FACE,{"derivedFrom":[makeQuery(id+"F1.opExtrude","CAP_FACE",FACE,{"disambiguationData":[OSD([sQuery(id+"F0.wireOp",EDGE,"E0"),sQuery(id+"F0.wireOp",EDGE,"E1"),sQuery(id+"F0.wireOp",EDGE,"E2"),sQuery(id+"F0.wireOp",EDGE,"E3.0"),sQuery(id+"F0.wireOp",EDGE,"E4"),sQuery(id+"F0.wireOp",EDGE,"E5")])],"isStart":false}),makeQuery(id+"F10.opExtrude","CAP_FACE",FACE,{"disambiguationData":[OSD([sQuery(id+"F9.wireOp",EDGE,"E13.bottom"),sQuery(id+"F9.wireOp",EDGE,"E13.top"),sQuery(id+"F9.wireOp",EDGE,"E13.left"),sQuery(id+"F9.wireOp",EDGE,"E13.right")])],"isStart":true})]});
            var sketch = newSketch(context, id + "F34", { "sketchPlane" : qUnion([Q0])});
            skLineSegment(sketch, "E42.bottom", {"start": v(-0.87, 10.31) * mm, "end": v(3.32, 10.31) * mm});
            skLineSegment(sketch, "E42.top", {"start": v(-0.87, 3.5) * mm, "end": v(3.32, 3.5) * mm});
            skLineSegment(sketch, "E42.right", {"start": v(3.32, 10.31) * mm, "end": v(3.32, 3.5) * mm});
            skLineSegment(sketch, "E43", {"start": v(-0.87, 10.31) * mm, "end": v(-0.87, 3.5) * mm});
            skSolve(sketch);
        }
        {
            var Q0;
            {var subQ1=makeQuery(id+"F1.opExtrude","CAP_EDGE",EDGE,{"disambiguationData":[OSD([sQuery(id+"F0.wireOp",EDGE,"E0")])],"isStart":false});var subQ6=sQuery(id+"F34.wireOp",EDGE,"E42.right");var subQ7=makeQuery(id+"F34.imprint","INTERSECT",VERTEX,{"derivedFrom":[subQ1,subQ6]});Q0=makeQuery(id+"F34.imprint","IMPRINT",FACE,{"disambiguationData":[TD([[makeQuery(id+"F34.imprint","IMPRINT",EDGE,{"disambiguationData":[TD([[subQ7,-1.0]])],"derivedFrom":subQ1}),1.0]])]});}
            var Q1;
            {var subQ0=sQuery(id+"F34.wireOp",EDGE,"E42.top");Q1=makeQuery(id+"F34.imprint","IMPRINT",FACE,{"disambiguationData":[TD([[makeQuery(id+"F34.imprint","IMPRINT",EDGE,{"derivedFrom":subQ0}),1.0]])]});}
            extrude(context, id + "F35", {"entities" : qUnion([Q0, Q1]), "operationType" : NewBodyOperationType.REMOVE, "depth" : 10.48 * mm, "offsetDistance" : 25 * mm});
        }
        {
            var Q0;
            {var subQ0=sQuery(id+"F9.wireOp",EDGE,"E13.left");var subQ1=sQuery(id+"F0.wireOp",EDGE,"E4");Q0=makeQuery(id+"F30.opBoolean","MERGE",FACE,{"derivedFrom":[makeQuery(id+"F21.boolean.opBoolean","MERGE",FACE,{"derivedFrom":[makeQuery(id+"F16.boolean.opBoolean","MERGE",FACE,{"derivedFrom":[makeQuery(id+"F10.boolean.opBoolean","MERGE",FACE,{"derivedFrom":[makeQuery(id+"F1.opExtrude","CAP_FACE",FACE,{"disambiguationData":[OSD([sQuery(id+"F0.wireOp",EDGE,"E0"),sQuery(id+"F0.wireOp",EDGE,"E1"),sQuery(id+"F0.wireOp",EDGE,"E2"),sQuery(id+"F0.wireOp",EDGE,"E3.0"),subQ1,sQuery(id+"F0.wireOp",EDGE,"E5")])],"isStart":true}),makeQuery(id+"F10.opExtrude","CAP_FACE",FACE,{"disambiguationData":[OSD([sQuery(id+"F9.wireOp",EDGE,"E13.bottom"),sQuery(id+"F9.wireOp",EDGE,"E13.top"),subQ0,sQuery(id+"F9.wireOp",EDGE,"E13.right")])],"isStart":false})]}),makeQuery(id+"F16.opSweep","SWEPT_FACE",FACE,{"disambiguationData":[OSD([subQ1,subQ0,sQuery(id+"F11.wireOp",EDGE,"E16")])]})]}),makeQuery(id+"F21.opExtrude","CAP_FACE",FACE,{"disambiguationData":[OSD([sQuery(id+"F20.wireOp",EDGE,"E24"),sQuery(id+"F20.wireOp",EDGE,"E25"),sQuery(id+"F20.wireOp",EDGE,"E26")])],"isStart":false})]}),makeQuery(id+"F29.opExtrude","CAP_FACE",FACE,{"disambiguationData":[OSD([sQuery(id+"F24.wireOp",EDGE,"E28.right"),sQuery(id+"F24.wireOp",EDGE,"E29.right"),sQuery(id+"F24.wireOp",EDGE,"E30"),sQuery(id+"F24.wireOp",EDGE,"E31")])],"isStart":false})]});}
            var sketch = newSketch(context, id + "F36", { "sketchPlane" : qUnion([Q0])});
            skLineSegment(sketch, "E44", {"start": v(6.02, 0.25) * mm, "end": v(6.7, 6) * mm});
            skLineSegment(sketch, "E45", {"start": v(6.7, 6) * mm, "end": v(5.2, 6) * mm});
            skLineSegment(sketch, "E46", {"start": v(5.2, 6) * mm, "end": v(6.02, 0.25) * mm});
            skSolve(sketch);
        }
        {
            var Q0;
            Q0 = qSketchRegion(id + "F36", true);
            extrude(context, id + "F37", {"entities" : qUnion([Q0]), "operationType" : NewBodyOperationType.REMOVE, "oppositeDirection" : true, "depth" : 25 * mm, "offsetDistance" : 25 * mm});
        }
        {
            var Q0;
            Q0=makeQuery(id+"F28.boolean.opBoolean","SPLIT",EDGE,{"derivedFrom":makeQuery(id+"F27.boolean.opBoolean","MERGE",EDGE,{"derivedFrom":[makeQuery(id+"F10.boolean.opBoolean","MERGE",EDGE,{"derivedFrom":[makeQuery(id+"F1.opExtrude","CAP_EDGE",EDGE,{"disambiguationData":[OSD([sQuery(id+"F0.wireOp",EDGE,"E4")])],"isStart":false}),makeQuery(id+"F10.opExtrude","CAP_EDGE",EDGE,{"disambiguationData":[OSD([sQuery(id+"F9.wireOp",EDGE,"E13.left")])],"isStart":true})]}),makeQuery(id+"F27.opExtrude","SWEPT_EDGE",EDGE,{"disambiguationData":[OSD([sQuery(id+"F9.wireOp",EDGE,"E13.top"),sQuery(id+"F26.wireOp",EDGE,"E34"),sQuery(id+"F26.wireOp",EDGE,"E36")])]})]})});
            var Q1;
            {var subQ0=sQuery(id+"F0.wireOp",EDGE,"E1");Q1=makeQuery(id+"F33.boolean.opBoolean","MERGE",EDGE,{"derivedFrom":[makeQuery(id+"F1.opExtrude","CAP_EDGE",EDGE,{"disambiguationData":[OSD([subQ0])],"isStart":false}),makeQuery(id+"F33.opSweep","CAP_EDGE",EDGE,{"disambiguationData":[OSD([subQ0,sQuery(id+"F9.wireOp",EDGE,"E13.top"),sQuery(id+"F26.wireOp",EDGE,"E34"),sQuery(id+"F26.wireOp",EDGE,"E36")])],"isStart":true})]});}
            fillet(context, id + "F38", {"entities" : qUnion([Q0, Q1]), "radius" : 0.25 * mm, "tangentPropagation" : true, "allowEdgeOverflow" : false});
        }
        {
            var Q0;
            Q0=makeQuery(id+"F21.boolean.opBoolean","MERGE",FACE,{"derivedFrom":[makeQuery(id+"F16.opSweep","SWEPT_FACE",FACE,{"disambiguationData":[OSD([sQuery(id+"F0.wireOp",EDGE,"E4"),sQuery(id+"F9.wireOp",EDGE,"E13.left"),sQuery(id+"F11.wireOp",EDGE,"E14")])]}),makeQuery(id+"F21.opExtrude","CAP_FACE",FACE,{"disambiguationData":[OSD([sQuery(id+"F20.wireOp",EDGE,"E24"),sQuery(id+"F20.wireOp",EDGE,"E25"),sQuery(id+"F20.wireOp",EDGE,"E26")])],"isStart":true})]});
            var sketch = newSketch(context, id + "F39", { "sketchPlane" : qUnion([Q0])});
            skLineSegment(sketch, "E47", {"start": v(4.24, 4.5) * mm, "end": v(5.05, 5.1) * mm});
            skLineSegment(sketch, "E48", {"start": v(4.24, 4.5) * mm, "end": v(5.43, 2.9) * mm});
            skLineSegment(sketch, "E49", {"start": v(5.43, 2.9) * mm, "end": v(6.24, 3.5) * mm});
            skLineSegment(sketch, "E50", {"start": v(6.24, 3.5) * mm, "end": v(5.05, 5.1) * mm});
            skSolve(sketch);
        }
        {
            var Q0;
            Q0 = qSketchRegion(id + "F39", true);
            var Q1;
            {var subQ0=sQuery(id+"F39.wireOp",EDGE,"j5K5fLT6-kDfy-4opf-k8Ae-rQ7NcVJ3yfoo");Q1=makeQuery(id+"F39.imprint","IMPRINT",FACE,{"disambiguationData":[TD([[makeQuery(id+"F39.imprint","IMPRINT",EDGE,{"derivedFrom":subQ0}),-1.0]])]});}
            extrude(context, id + "F40", {"entities" : qUnion([Q0, Q1]), "operationType" : NewBodyOperationType.ADD, "depth" : 1 * mm, "offsetDistance" : 25 * mm});
        }
        {
            var Q0;
            Q0=makeQuery(id+"F40.opExtrude","SWEPT_EDGE",EDGE,{"disambiguationData":[OSD([sQuery(id+"F39.wireOp",EDGE,"E48"),sQuery(id+"F39.wireOp",EDGE,"E49")])]});
            var Q1;
            Q1=makeQuery(id+"F40.opExtrude","SWEPT_EDGE",EDGE,{"disambiguationData":[OSD([sQuery(id+"F39.wireOp",EDGE,"E49"),sQuery(id+"F39.wireOp",EDGE,"E50")])]});
            var Q2;
            Q2=makeQuery(id+"F40.opExtrude","SWEPT_EDGE",EDGE,{"disambiguationData":[OSD([sQuery(id+"F39.wireOp",EDGE,"E47"),sQuery(id+"F39.wireOp",EDGE,"E48")])]});
            var Q3;
            Q3=makeQuery(id+"F40.opExtrude","SWEPT_EDGE",EDGE,{"disambiguationData":[OSD([sQuery(id+"F39.wireOp",EDGE,"E47"),sQuery(id+"F39.wireOp",EDGE,"E50")])]});
            fillet(context, id + "F41", {"entities" : qUnion([Q0, Q1, Q2, Q3]), "radius" : 0.2 * mm, "tangentPropagation" : true, "allowEdgeOverflow" : false});
        }
    });
